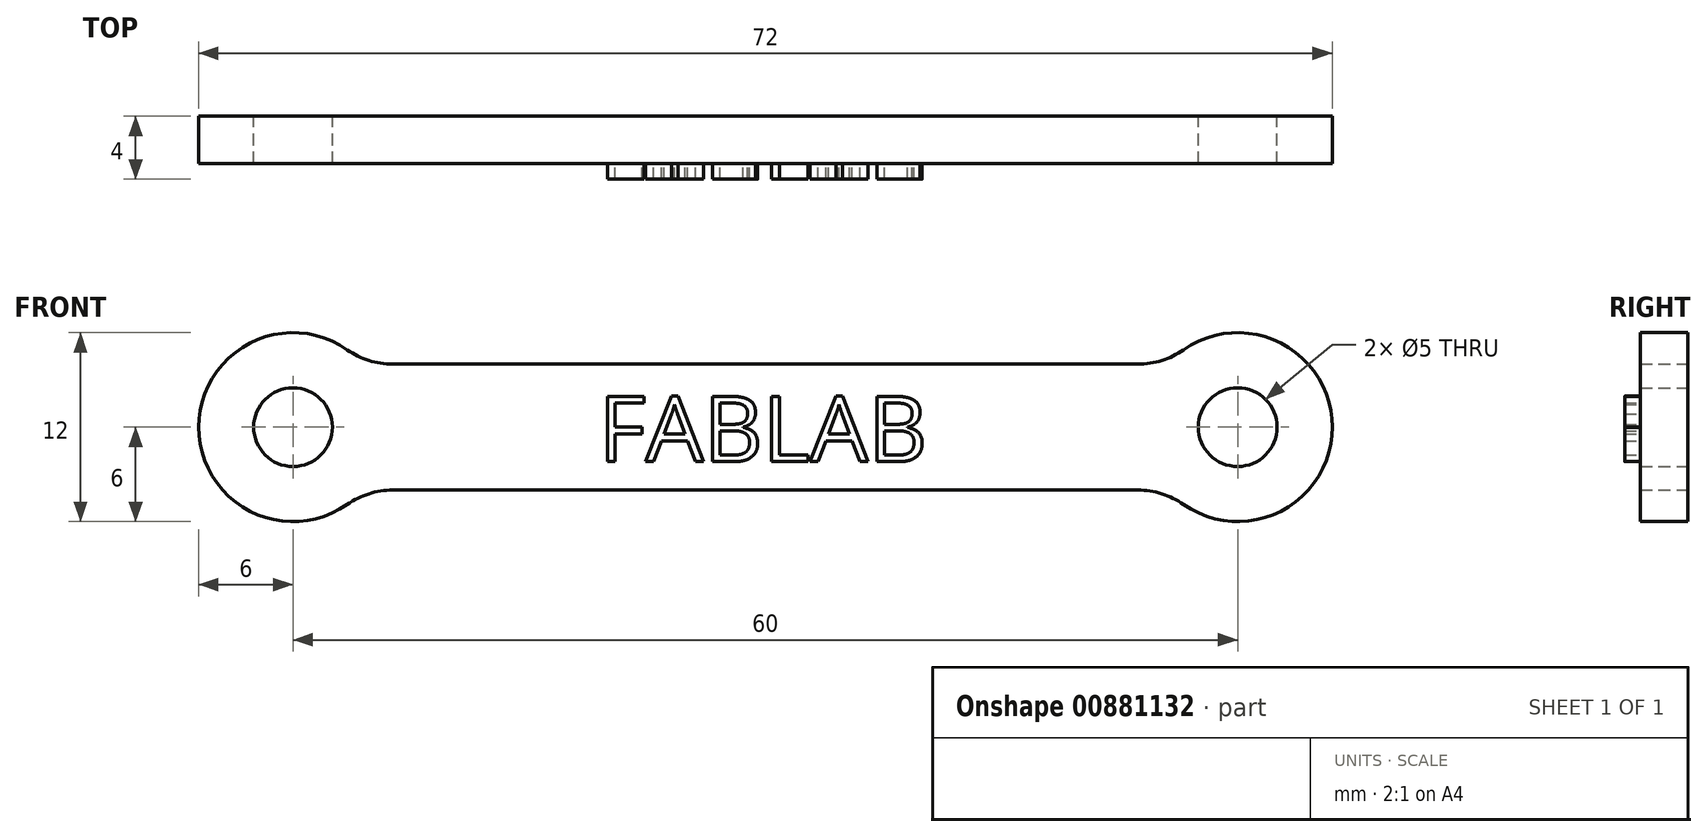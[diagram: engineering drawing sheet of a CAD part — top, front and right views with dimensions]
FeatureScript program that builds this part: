
annotation { "Feature Type Name" : "Feature", "Feature Type Description" : "" }
export const myFeature = defineFeature(function(context is Context, id is Id, definition is map)
    precondition{}
    {
        {
            var Q0;
            Q0=qCreatedBy(makeId("Front.planeOp"),FACE);
            var sketch = newSketch(context, id + "F0", { "sketchPlane" : qUnion([Q0])});
            skArc(sketch, "E0", {"start": v(3.45, 4.9) * mm, "mid": v(-6, 0) * mm, "end": v(3.45, -4.9) * mm});
            skCircle(sketch, "E1", {"center": v(0, 0) * mm, "radius": 2.5 * mm});
            skCircle(sketch, "E2", {"center": v(60, 0) * mm, "radius": 2.5 * mm});
            skArc(sketch, "E3", {"start": v(56.55, -4.9) * mm, "mid": v(66, 0) * mm, "end": v(56.55, 4.9) * mm});
            skLineSegment(sketch, "E4", {"start": v(6.32, 4) * mm, "end": v(53.68, 4) * mm});
            skLineSegment(sketch, "E5", {"start": v(6.32, -4) * mm, "end": v(53.68, -4) * mm});
            skPoint(sketch, "E6.visualSharp", {"position": v(4.47, 4) * mm});
            skArc(sketch, "E6.filletArc", {"start": v(3.45, 4.9) * mm, "mid": v(4.82, 4.23) * mm, "end": v(6.32, 4) * mm});
            skPoint(sketch, "E7.visualSharp", {"position": v(4.47, -4) * mm});
            skArc(sketch, "E7.filletArc", {"start": v(6.32, -4) * mm, "mid": v(4.82, -4.23) * mm, "end": v(3.45, -4.9) * mm});
            skPoint(sketch, "E8.visualSharp", {"position": v(55.53, -4) * mm});
            skArc(sketch, "E8.filletArc", {"start": v(56.55, -4.9) * mm, "mid": v(55.18, -4.23) * mm, "end": v(53.68, -4) * mm});
            skPoint(sketch, "E9.visualSharp", {"position": v(55.53, 4) * mm});
            skArc(sketch, "E9.filletArc", {"start": v(53.68, 4) * mm, "mid": v(55.18, 4.23) * mm, "end": v(56.55, 4.9) * mm});
            skSolve(sketch);
        }
        {
            var Q0;
            Q0=makeQuery(id+"F0.imprint","IMPRINT",FACE,{"disambiguationData":[TD([[makeQuery(id+"F0.imprint","IMPRINT",EDGE,{"derivedFrom":sQuery(id+"F0.wireOp",EDGE,"E0")}),1.0]])]});
            extrude(context, id + "F1", {"entities" : qUnion([Q0]), "depth" : 3 * mm, "offsetDistance" : 25 * mm});
        }
        {
            var Q0;
            Q0=makeQuery(id+"F1.opExtrude","CAP_FACE",FACE,{"disambiguationData":[OSD([sQuery(id+"F0.wireOp",EDGE,"E0"),sQuery(id+"F0.wireOp",EDGE,"E1"),sQuery(id+"F0.wireOp",EDGE,"E2"),sQuery(id+"F0.wireOp",EDGE,"E3"),sQuery(id+"F0.wireOp",EDGE,"E4"),sQuery(id+"F0.wireOp",EDGE,"E5"),sQuery(id+"F0.wireOp",EDGE,"E6.filletArc"),sQuery(id+"F0.wireOp",EDGE,"E7.filletArc"),sQuery(id+"F0.wireOp",EDGE,"E8.filletArc"),sQuery(id+"F0.wireOp",EDGE,"E9.filletArc")])],"isStart":false});
            var sketch = newSketch(context, id + "F2", { "sketchPlane" : qUnion([Q0])});
            skText(sketch, "E10", { "text": "FABLAB", "fontName": "OpenSans-Regular.ttf"});
            const initialGuessF2  = {"E10": [0.0194, -0.00219, 1, 0, 0.00418]};
            skSetInitialGuess(sketch, initialGuessF2);
            skSolve(sketch);
        }
        {
            var Q0;
            Q0 = qSketchRegion(id + "F2", true);
            extrude(context, id + "F3", {"entities" : qUnion([Q0]), "operationType" : NewBodyOperationType.ADD, "depth" : 1 * mm, "offsetDistance" : 25 * mm});
        }
    });
